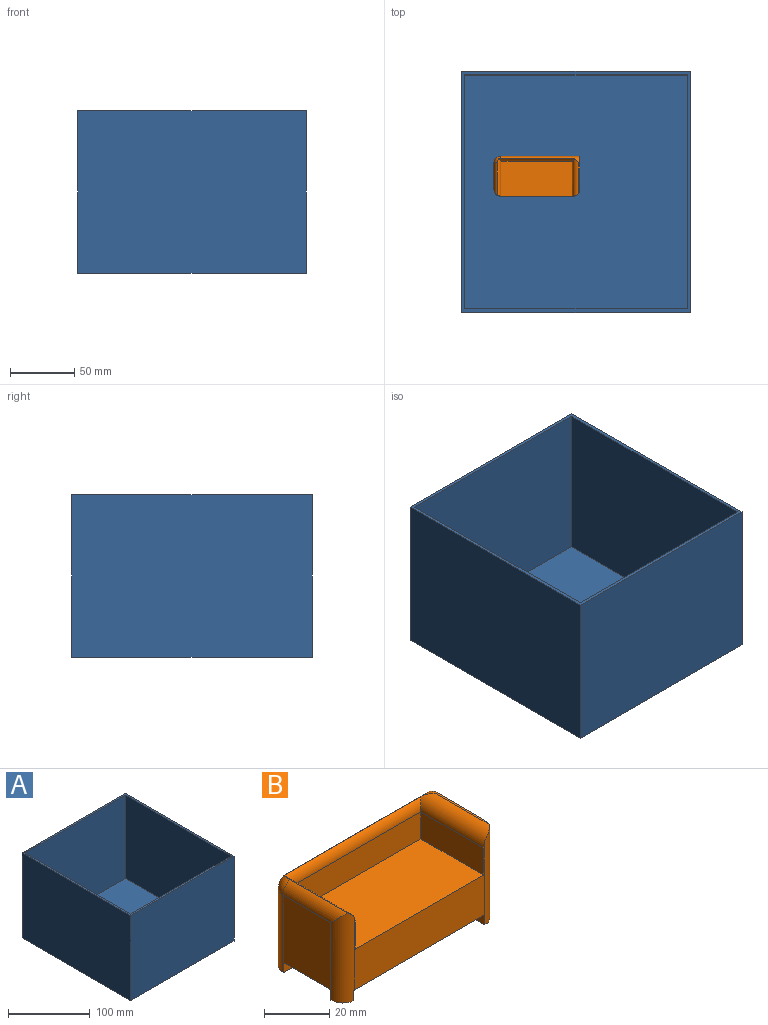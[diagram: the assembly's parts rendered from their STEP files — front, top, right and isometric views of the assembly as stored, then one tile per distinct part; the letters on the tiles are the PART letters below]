
ASSEMBLY  parts=2 mates=1
PART A: 11 faces, bbox 178.4x187.7x127 mm
  f0: plane 187.68x127mm, normal (1,0,0), area 23835.1mm2, adj f1,f3,f4,f5
  f1: plane 178.36x127mm, normal (0,1,0), area 22651.8mm2, adj f0,f2,f4,f5
  f2: plane 187.68x127mm, normal (-1,0,0), area 23835.1mm2, adj f1,f3,f4,f5
  f3: plane 178.36x127mm, normal (0,-1,0), area 22651.8mm2, adj f0,f2,f4,f5
  f4: plane 187.68x178.36mm, normal (0,0,1), area 1833.7mm2, adj f0,f1,f2,f3,f6,f7,f8,f9
  f5: plane 187.68x178.36mm, normal (0,0,-1), area 33474.4mm2, adj f0,f1,f2,f3
  f6: plane 182.6x124.46mm, normal (-1,0,0), area 22726.1mm2, adj f4,f7,f9,f10
  f7: plane 173.28x124.46mm, normal (0,-1,0), area 21566.6mm2, adj f4,f6,f8,f10
  f8: plane 182.6x124.46mm, normal (1,0,0), area 22726.1mm2, adj f4,f7,f9,f10
  f9: plane 173.28x124.46mm, normal (0,1,0), area 21566.6mm2, adj f4,f6,f8,f10
  f10: plane 182.6x173.28mm, normal (0,0,1), area 31640.7mm2, adj f6,f7,f8,f9
PART B: 31 faces, bbox 66.9x31x34.3 mm
  f0: plane 66.88x30.96mm, normal (0,0,-1), area 1965mm2, adj f1,f2,f3,f4,f18,f19,f21,f22
  f1: plane 61.8x29.21mm, normal (0,1,0), area 1589.6mm2, adj f0,f4,f11,f14,f25,f26
  f2: plane 29.21x20.8mm, normal (-1,0,0), area 529.8mm2, adj f0,f10,f11,f18,f20,f30
  f3: plane 56.72x27.83mm, normal (0,-1,0), area 875.9mm2, adj f0,f6,f8,f9,f12,f15,f17,f30
  f4: plane 34.29x25.88mm, normal (1,0,0), area 804.6mm2, adj f0,f1,f5,f14,f17,f22,f23,f24
  f5: plane 23.23x0.62mm, normal (0,0,1), area 13.9mm2, adj f4,f14,f15,f17
  f6: plane 27.25x10.16mm, normal (-1,0,0), area 276.8mm2, adj f3,f7,f9,f15
  f7: plane 55.73x10.16mm, normal (0,-1,0), area 566.3mm2, adj f6,f8,f9,f16
  f8: plane 27.25x10.16mm, normal (1,0,0), area 276.8mm2, adj f3,f7,f9,f12
  f9: plane 55.73x27.25mm, normal (0,0,1), area 1518.7mm2, adj f3,f6,f7,f8
  f10: cylinder r=5.08mm len=25.3mm, axis (0,1,0), area 128.9mm2, adj f2,f12,f13,f30
  f11: cylinder r=5.08mm len=29.21mm, axis (0,0,-1), area 233.1mm2, adj f1,f2,f13,f27,f28,f29
  f12: cylinder r=5.08mm len=28.97mm, axis (0,1,0), area 153.6mm2, adj f3,f8,f10,f13,f16,f30
  f13: sphere r=5.08mm, area 33.5mm2, adj f10,f11,f12,f14,f16
  f14: cylinder r=5.08mm len=61.8mm, axis (1,0,0), area 285.5mm2, adj f1,f4,f5,f13,f15,f16
  f15: cylinder r=5.08mm len=29.11mm, axis (0,-1,0), area 217.8mm2, adj f3,f5,f6,f14,f16,f17
  f16: cylinder r=5.08mm len=59.31mm, axis (1,0,0), area 255.8mm2, adj f7,f12,f13,f14,f15
  f17: cylinder r=5.08mm len=34.29mm, axis (0,0,-1), area 270.1mm2, adj f3,f4,f5,f15,f21,f23
  f18: plane 4.71x3.81mm, normal (0,1,0), area 17.9mm2, adj f0,f2,f19,f20
  f19: plane 5.44x3.81mm, normal (1,0,0), area 20.7mm2, adj f0,f18,f20,f30
  f20: plane 5.44x4.71mm, normal (0,0,-1), area 20.1mm2, adj f2,f18,f19,f30
  f21: plane 5.45x3.81mm, normal (-1,-0.02,0), area 20.8mm2, adj f0,f17,f22,f23
  f22: plane 5.2x3.81mm, normal (0,1,0), area 19.8mm2, adj f0,f4,f21,f23
  f23: plane 5.45x5.2mm, normal (0,0,-1), area 22.5mm2, adj f4,f17,f21,f22
  f24: plane 5.2x3.81mm, normal (0,-1,0), area 19.8mm2, adj f0,f4,f25,f26
  f25: plane 5.2x3.81mm, normal (-1,0,0), area 19.8mm2, adj f0,f1,f24,f26
  f26: plane 5.2x5.2mm, normal (0,0,-1), area 27.1mm2, adj f1,f4,f24,f25
  f27: plane 5.2x3.81mm, normal (1,-0.07,0), area 19.9mm2, adj f0,f11,f28,f29
  f28: plane 4.71x3.81mm, normal (-0.03,-1,0), area 17.9mm2, adj f0,f11,f27,f29
  f29: plane 5.2x5.08mm, normal (0,0,-1), area 19.6mm2, adj f11,f27,f28
  f30: cylinder r=5.08mm len=33.71mm, axis (0,0,1), area 254.2mm2, adj f0,f2,f3,f10,f12,f19,f20
PLACE A t=(-23.27,121.44,100.23)mm fixed
PLACE B t=(-87.22,118.31,106.58)mm
MATE fastened B.f23 <-> A.f10  axis (0,0,-1) through (-23.27,121.44,102.77)mm
